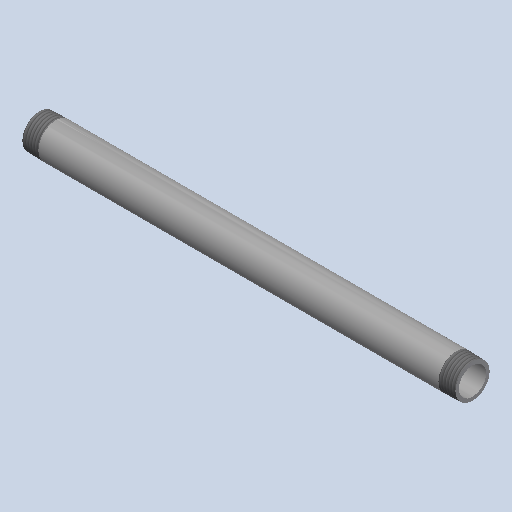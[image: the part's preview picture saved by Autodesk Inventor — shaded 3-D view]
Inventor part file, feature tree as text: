
AUTODESK INVENTOR PART (.ipt)
format: ipt  version: 2025 (Build 290162000, 162)  size: 162,816 bytes
history: native  units: mm (DEFAULTED — no unit token found)
features: other x8, revolve x1
ambient origin geometry x8: Origin, YZ Plane, XZ Plane, XY Plane, X Axis, Y Axis, Z Axis, Center Point
bodies: Solid1 (feature_tree)
feature tree (9):
  revolve  "Revolution1"  [1 undecoded]
  other  "Work Axis1"
  other  "Work Point5"
  other  "Work Axis2"
  other  "Work Point6"
  other  "Work Axis3"
  other  "Work Axis4"
  other  "Work Point7"
  other  "Work Point8"
note: 1 required parameter value undecoded (feature->parameter linkage not recoverable at this tier; creation-order binding heuristic only, values carry confidence <= 0.55)
